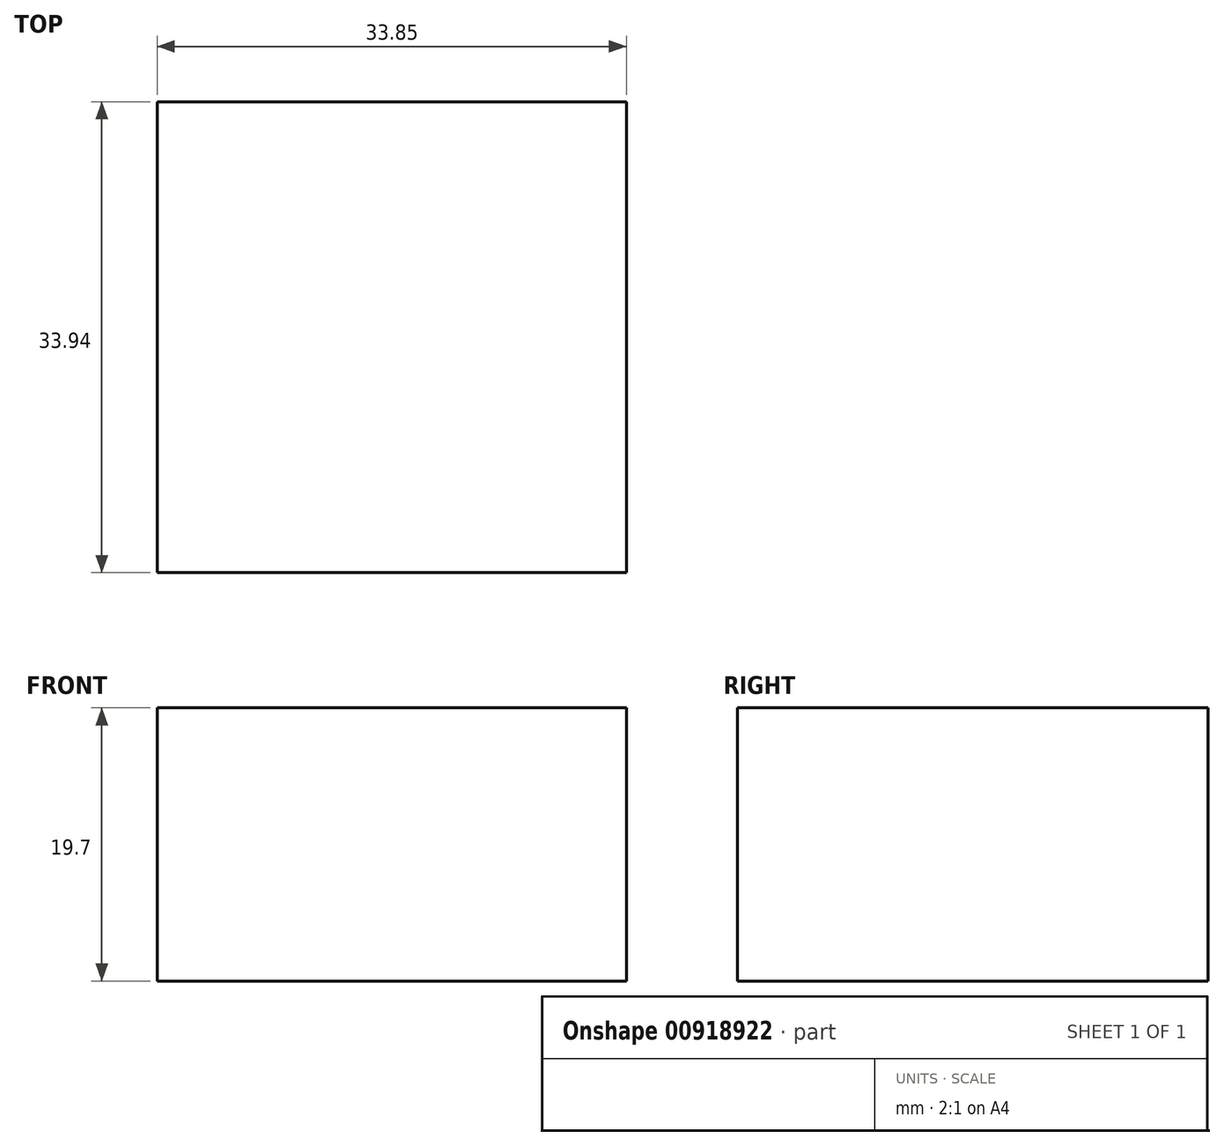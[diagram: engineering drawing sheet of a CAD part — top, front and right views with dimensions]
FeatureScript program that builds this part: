
annotation { "Feature Type Name" : "Feature", "Feature Type Description" : "" }
export const myFeature = defineFeature(function(context is Context, id is Id, definition is map)
    precondition{}
    {
        {
            var Q0;
            Q0=qCreatedBy(makeId("Top.planeOp"),FACE);
            var sketch = newSketch(context, id + "F0", { "sketchPlane" : qUnion([Q0])});
            skLineSegment(sketch, "E0.bottom", {"start": v(0, 0) * mm, "end": v(33.85, 0) * mm});
            skLineSegment(sketch, "E0.top", {"start": v(0, 33.94) * mm, "end": v(33.85, 33.94) * mm});
            skLineSegment(sketch, "E0.left", {"start": v(0, 0) * mm, "end": v(0, 33.94) * mm});
            skLineSegment(sketch, "E0.right", {"start": v(33.85, 0) * mm, "end": v(33.85, 33.94) * mm});
            skSolve(sketch);
        }
        {
            var Q0;
            Q0=makeQuery(id+"F0.imprint","IMPRINT",FACE,{"disambiguationData":[TD([[makeQuery(id+"F0.imprint","IMPRINT",EDGE,{"derivedFrom":sQuery(id+"F0.wireOp",EDGE,"E0.bottom")}),1.0]])]});
            extrude(context, id + "F1", {"entities" : qUnion([Q0]), "depth" : 19.7 * mm, "offsetDistance" : 25 * mm});
        }
    });
